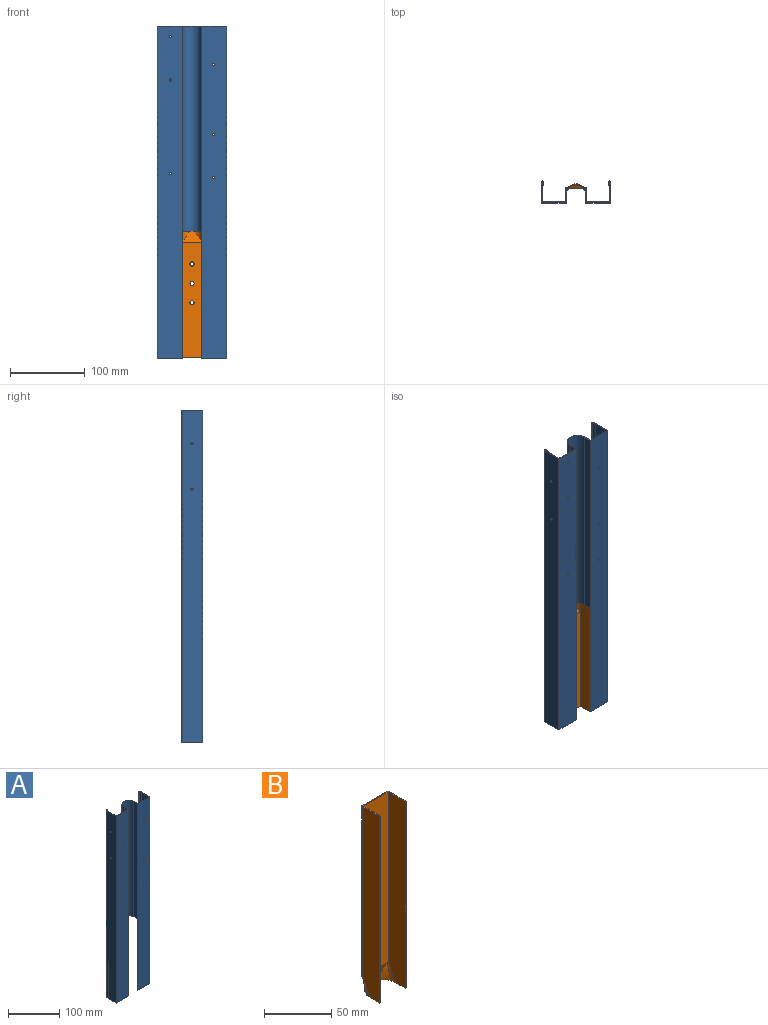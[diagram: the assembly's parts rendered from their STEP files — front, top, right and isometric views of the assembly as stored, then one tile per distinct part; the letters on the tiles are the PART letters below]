
ASSEMBLY  parts=2 mates=1
PART A: 38 faces, bbox 93x29x445 mm
  f0: plane 445x11mm, normal (1,0,0), area 3195mm2, adj f1,f6,f9,f19,f25,f37
  f1: cylinder r=13mm len=275mm, axis (0,0,-1), area 11231.2mm2, adj f0,f2,f25,f37
  f2: plane 445x11mm, normal (-1,0,0), area 3195mm2, adj f1,f10,f18,f25,f26,f37
  f3: plane 275x10mm, normal (1,0,0), area 2750mm2, adj f4,f18,f25,f37
  f4: cylinder r=14mm len=275mm, axis (0,0,-1), area 12095.1mm2, adj f3,f5,f25,f37
  f5: plane 275x10mm, normal (-1,0,0), area 2750mm2, adj f4,f19,f25,f37
  f6: plane 33.5x29mm, normal (0,0,-1), area 68.6mm2, adj f0,f7,f8,f9,f19,f20,f21,f22
  f7: cylinder r=1.5mm len=445mm, axis (0,0,-1), area 2209.5mm2, adj f6,f8,f24,f25
  f8: plane 445x27.5mm, normal (-1,0,0), area 12223.4mm2, adj f6,f7,f9,f25,f32,f33
  f9: plane 445x33.5mm, normal (0,-1,0), area 14886.3mm2, adj f0,f6,f8,f25,f27,f28,f34
  f10: plane 445x33.5mm, normal (0,-1,0), area 14886.3mm2, adj f2,f11,f25,f26,f29,f35,f36
  f11: plane 445x27.5mm, normal (1,0,0), area 12223.4mm2, adj f10,f12,f25,f26,f30,f31
  f12: cylinder r=1.5mm len=445mm, axis (0,0,-1), area 2209.5mm2, adj f11,f13,f25,f26
  f13: plane 445x5.25mm, normal (-0.99,-0.17,0), area 2369.1mm2, adj f12,f14,f25,f26
  f14: plane 445x0.99mm, normal (0.17,-0.99,0), area 445mm2, adj f13,f15,f25,f26
  f15: plane 445x5.25mm, normal (0.99,0.17,0), area 2369.1mm2, adj f14,f16,f25,f26
  f16: cylinder r=0.5mm len=445mm, axis (0,0,-1), area 736.5mm2, adj f15,f17,f25,f26
  f17: plane 445x26.5mm, normal (-1,0,0), area 11778.4mm2, adj f16,f18,f25,f26,f30,f31
  f18: plane 445x32.5mm, normal (0,1,0), area 14166.3mm2, adj f2,f3,f17,f25,f26,f29,f35,f36
  f19: plane 445x32.5mm, normal (0,1,0), area 14166.3mm2, adj f0,f5,f6,f20,f25,f27,f28,f34
  f20: plane 445x26.5mm, normal (1,0,0), area 11778.4mm2, adj f6,f19,f21,f25,f32,f33
  f21: cylinder r=0.5mm len=445mm, axis (0,0,-1), area 736.5mm2, adj f6,f20,f22,f25
  f22: plane 445x5.25mm, normal (-0.99,0.17,0), area 2369.1mm2, adj f6,f21,f23,f25
  f23: plane 445x0.99mm, normal (-0.17,-0.99,0), area 445mm2, adj f6,f22,f24,f25
  f24: plane 445x5.25mm, normal (0.99,-0.17,0), area 2369.1mm2, adj f6,f7,f23,f25
  f25: plane 93x29mm, normal (0,0,1), area 199.7mm2, adj f0,f1,f2,f3,f4,f5,f7,f8
  f26: plane 33.5x29mm, normal (0,0,-1), area 68.6mm2, adj f2,f10,f11,f12,f13,f14,f15,f16
  f27: cylinder r=1.5mm len=3mm, axis (0,-1,0), area 9.4mm2, adj f9,f19
  f28: cylinder r=1.5mm len=3mm, axis (0,-1,0), area 9.4mm2, adj f9,f19
  f29: cylinder r=1.5mm len=3mm, axis (0,-1,0), area 9.4mm2, adj f10,f18
  f30: cylinder r=1.5mm len=3mm, axis (-1,0,0), area 9.4mm2, adj f11,f17
  f31: cylinder r=1.5mm len=3mm, axis (-1,0,0), area 9.4mm2, adj f11,f17
  f32: cylinder r=1.5mm len=3mm, axis (-1,0,0), area 9.4mm2, adj f8,f20
  f33: cylinder r=1.5mm len=3mm, axis (-1,0,0), area 9.4mm2, adj f8,f20
  f34: cylinder r=1.5mm len=3mm, axis (0,-1,0), area 9.4mm2, adj f9,f19
  f35: cylinder r=1.5mm len=3mm, axis (0,-1,0), area 9.4mm2, adj f10,f18
  f36: cylinder r=1.5mm len=3mm, axis (0,-1,0), area 9.4mm2, adj f10,f18
  f37: plane 28x24mm, normal (0,0,-1), area 62.4mm2, adj f0,f1,f2,f3,f4,f5,f18,f19
PART B: 27 faces, bbox 35.2x31.2x177.2 mm
  f0: cylinder r=2.75mm len=5.5mm, axis (0,1,0), area 17.3mm2, adj f5,f17
  f1: cylinder r=2.75mm len=5.5mm, axis (0,1,0), area 17.3mm2, adj f5,f17
  f2: cylinder r=2.75mm len=5.5mm, axis (0,1,0), area 17.3mm2, adj f5,f17
  f3: cylinder r=2mm len=155mm, axis (0,0,1), area 76mm2, adj f5,f7,f12,f13
  f4: cylinder r=2mm len=155mm, axis (0,0,1), area 76mm2, adj f5,f10,f11,f13
  f5: plane 155.16x25.88mm, normal (0,-1,0), area 3944.4mm2, adj f0,f1,f2,f3,f4,f6,f7,f11
  f6: plane 31.84x20.86mm, normal (0,-0.95,-0.32), area 252.1mm2, adj f5,f7,f8,f9,f11,f22
  f7: bspline ~15.36x9.22mm, area 39.2mm2, adj f3,f5,f6,f8,f12,f22
  f8: bspline ~13.47x11.57mm, area 74.8mm2, adj f6,f7,f22
  f9: bspline ~13.47x11.57mm, area 74.8mm2, adj f6,f11,f22
  f10: plane 170x17.51mm, normal (1,0,0), area 2921.1mm2, adj f4,f11,f13,f22,f23
  f11: bspline ~15.36x9.22mm, area 39.2mm2, adj f4,f5,f6,f9,f10,f22
  f12: plane 170x17.51mm, normal (-1,0,0), area 2921.1mm2, adj f3,f7,f13,f14,f22
  f13: plane 28x19mm, normal (0,0,1), area 63.6mm2, adj f3,f4,f5,f10,f12,f14,f15,f16
  f14: plane 170x1mm, normal (0,-1,0), area 170mm2, adj f12,f13,f22,f26
  f15: cylinder r=3mm len=155mm, axis (0,0,1), area 240.9mm2, adj f13,f17,f19,f26
  f16: cylinder r=3mm len=155mm, axis (0,0,1), area 240.9mm2, adj f13,f17,f24,f25
  f17: plane 155x27.21mm, normal (0,1,0), area 4146.7mm2, adj f0,f1,f2,f13,f15,f16,f18
  f18: plane 34.37x22.16mm, normal (0,0.95,0.32), area 265.2mm2, adj f17,f19,f20,f21,f25
  f19: bspline ~15x9.97mm, area 49.2mm2, adj f15,f18,f20,f22,f26
  f20: bspline ~13.73x13.57mm, area 89.1mm2, adj f18,f19,f22
  f21: bspline ~13.7x13.48mm, area 89.1mm2, adj f18,f22,f25
  f22: plane 34.23x30.23mm, normal (0,0,-1), area 62.5mm2, adj f6,f7,f8,f9,f10,f11,f12,f14
  f23: plane 170x1mm, normal (0,-1,0), area 170mm2, adj f10,f13,f22,f24
  f24: plane 170x17.51mm, normal (-1,0,0), area 2921.1mm2, adj f13,f16,f22,f23,f25
  f25: bspline ~15x9.97mm, area 49.2mm2, adj f16,f18,f21,f22,f24
  f26: plane 170x17.51mm, normal (1,0,0), area 2921.1mm2, adj f13,f14,f15,f19,f22
PLACE A t=(-1.02,0.22,-791.81)mm fixed
PLACE B rot(axis=(0,1,0),180deg) t=(-1151.02,-429.78,-621.81)mm
MATE fastened B.f22 <-> A.f37  axis (0,0,1) through (-1137.02,-439.78,-621.81)mm
